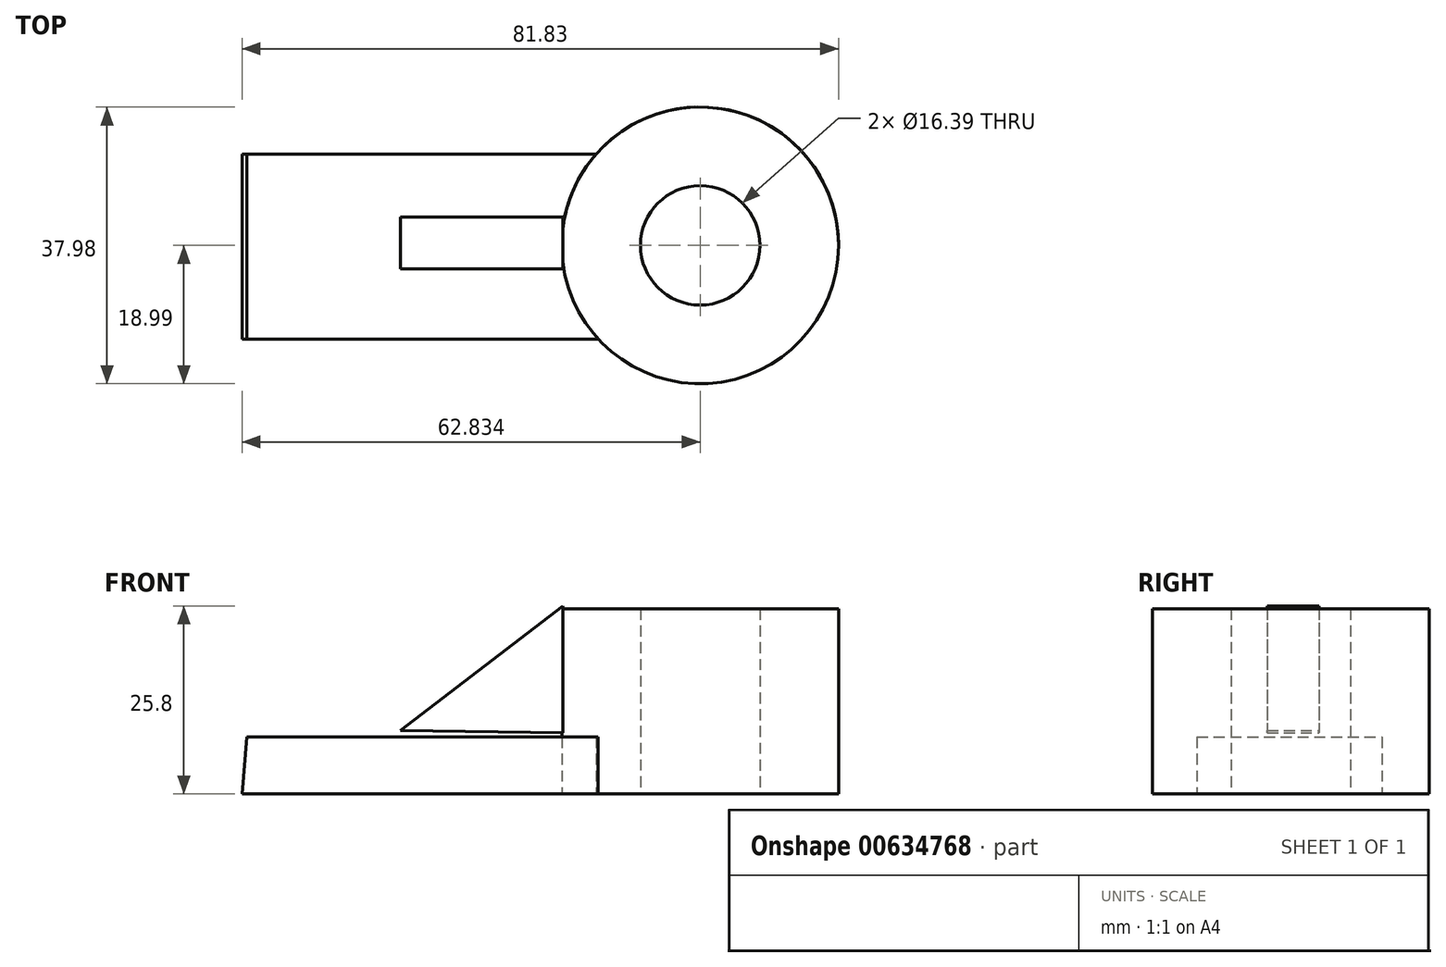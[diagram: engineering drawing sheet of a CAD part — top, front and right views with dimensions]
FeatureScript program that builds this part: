
annotation { "Feature Type Name" : "Feature", "Feature Type Description" : "" }
export const myFeature = defineFeature(function(context is Context, id is Id, definition is map)
    precondition{}
    {
        {
            var Q0;
            Q0=qCreatedBy(makeId("Front.planeOp"),FACE);
            var sketch = newSketch(context, id + "F0", { "sketchPlane" : qUnion([Q0])});
            skLineSegment(sketch, "E0", {"start": v(-70.4, 0) * mm, "end": v(-21.53, 0) * mm});
            skLineSegment(sketch, "E1", {"start": v(-21.53, 0) * mm, "end": v(-21.53, 7.79) * mm});
            skLineSegment(sketch, "E2", {"start": v(-21.53, 7.79) * mm, "end": v(-69.78, 7.79) * mm});
            skLineSegment(sketch, "E3", {"start": v(-69.78, 7.79) * mm, "end": v(-70.4, 0) * mm});
            skSolve(sketch);
        }
        {
            var Q0;
            Q0=makeQuery(id+"F0.imprint","IMPRINT",FACE,{"disambiguationData":[TD([[makeQuery(id+"F0.imprint","IMPRINT",EDGE,{"derivedFrom":sQuery(id+"F0.wireOp",EDGE,"E0")}),1.0]])]});
            extrude(context, id + "F1", {"entities" : qUnion([Q0]), "depth" : 25.4 * mm, "offsetDistance" : 25.4 * mm});
        }
        {
            var Q0;
            Q0=qCreatedBy(makeId("Top.planeOp"),FACE);
            var sketch = newSketch(context, id + "F2", { "sketchPlane" : qUnion([Q0])});
            skCircle(sketch, "E4", {"center": v(-7.56, -12.55) * mm, "radius": 19 * mm});
            skCircle(sketch, "E5", {"center": v(-7.56, -12.55) * mm, "radius": 8.2 * mm});
            skSolve(sketch);
        }
        {
            var Q0;
            Q0=makeQuery(id+"F2.imprint","IMPRINT",FACE,{"disambiguationData":[TD([[makeQuery(id+"F2.imprint","IMPRINT",EDGE,{"derivedFrom":sQuery(id+"F2.wireOp",EDGE,"E4")}),1.0]])]});
            extrude(context, id + "F3", {"entities" : qUnion([Q0]), "operationType" : NewBodyOperationType.ADD, "depth" : 25.4 * mm, "offsetDistance" : 25.4 * mm});
        }
        {
            var Q0;
            Q0=qCreatedBy(makeId("Front.planeOp"),FACE);
            var sketch = newSketch(context, id + "F4", { "sketchPlane" : qUnion([Q0])});
            skLineSegment(sketch, "E6", {"start": v(-26.42, 25.8) * mm, "end": v(-48.7, 8.7) * mm});
            skLineSegment(sketch, "E7", {"start": v(-26.42, 25.8) * mm, "end": v(-26.42, 8.4) * mm});
            skLineSegment(sketch, "E8", {"start": v(-26.42, 8.4) * mm, "end": v(-48.7, 8.7) * mm});
            skSolve(sketch);
        }
        {
            var Q0;
            Q0 = qSketchRegion(id + "F4", true);
            extrude(context, id + "F5", {"entities" : qUnion([Q0]), "operationType" : NewBodyOperationType.ADD, "depth" : 7.11 * mm, "offsetDistance" : 25.4 * mm});
        }
        {
            var Q0;
            Q0=makeQuery(id+"F5.opExtrude","SWEPT_BODY",BODY,{"disambiguationData":[OSD([sQuery(id+"F4.wireOp",EDGE,"E6"),sQuery(id+"F4.wireOp",EDGE,"E7"),sQuery(id+"F4.wireOp",EDGE,"E8")])]});
            transform(context, id + "F6", {"entities" : qUnion([Q0]), "transformType" : TransformType.TRANSLATION_3D, "dx" : 0 * mm, "dy" : -6.1 * mm, "dz" : 0 * mm, "makeCopy" : false});
        }
        {
            var Q0;
            Q0 = qSketchRegion(id + "F2", true);
            extrude(context, id + "F7", {"entities" : qUnion([Q0]), "depth" : 25.4 * mm, "offsetDistance" : 25.4 * mm});
        }
        {
            var Q0;
            Q0=makeQuery(id+"F5.opExtrude","SWEPT_BODY",BODY,{"disambiguationData":[OSD([sQuery(id+"F4.wireOp",EDGE,"E6"),sQuery(id+"F4.wireOp",EDGE,"E7"),sQuery(id+"F4.wireOp",EDGE,"E8")])]});
            transform(context, id + "F8", {"entities" : qUnion([Q0]), "transformType" : TransformType.TRANSLATION_3D, "dx" : 0 * mm, "dy" : -2.54 * mm, "dz" : 0 * mm, "makeCopy" : false});
        }
    });
